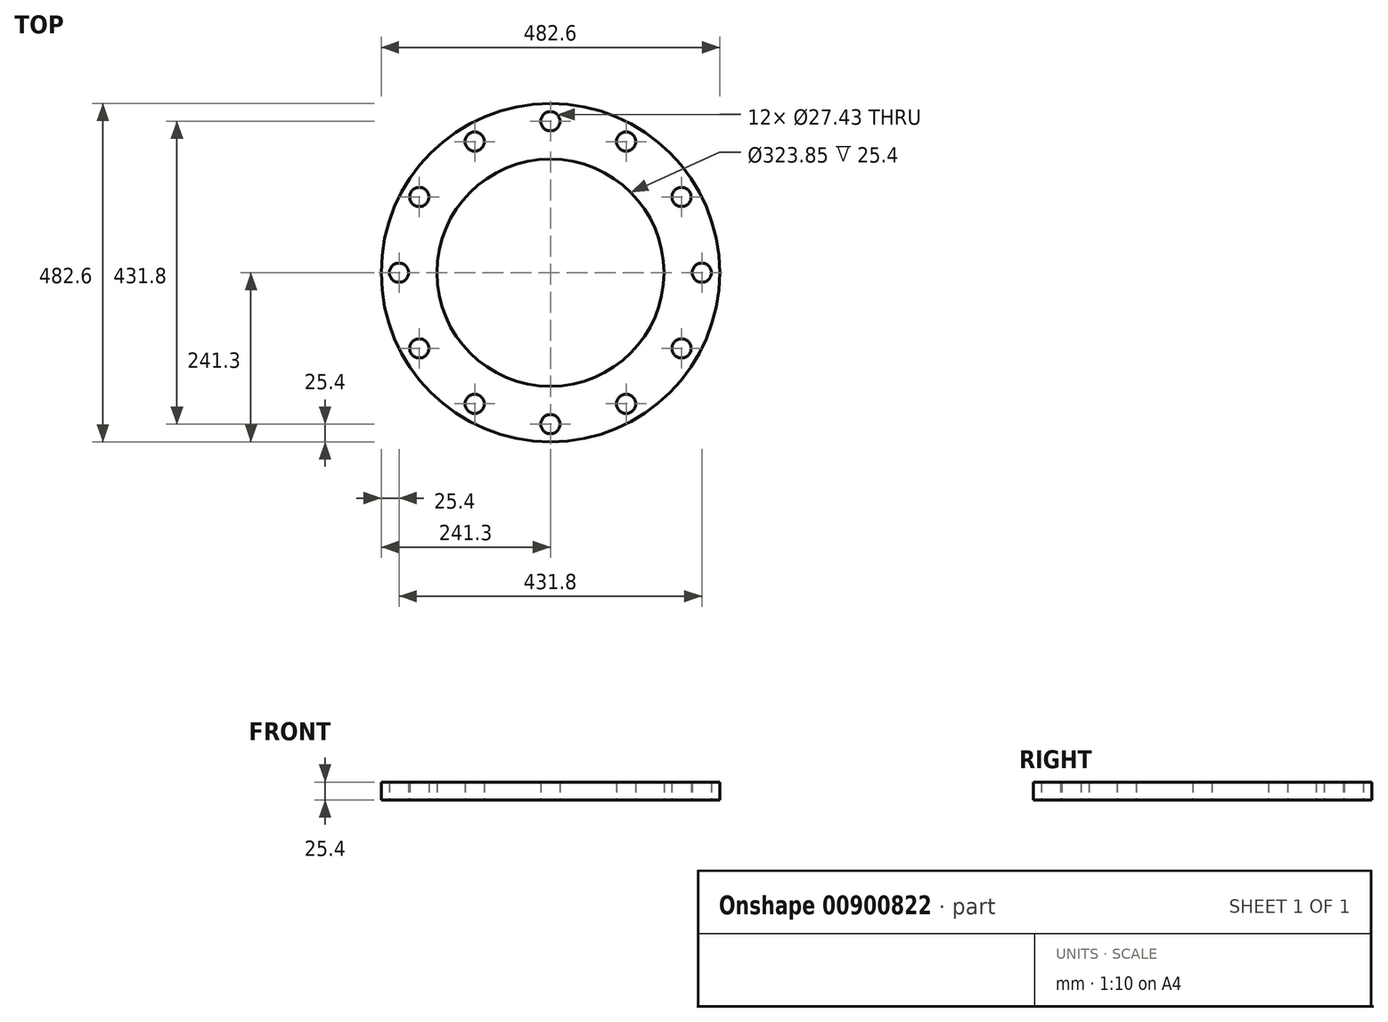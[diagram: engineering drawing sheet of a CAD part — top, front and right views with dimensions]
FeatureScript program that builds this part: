
annotation { "Feature Type Name" : "Feature", "Feature Type Description" : "" }
export const myFeature = defineFeature(function(context is Context, id is Id, definition is map)
    precondition{}
    {
        {
            var Q0;
            Q0=qCreatedBy(makeId("Top.planeOp"),FACE);
            var sketch = newSketch(context, id + "F0", { "sketchPlane" : qUnion([Q0])});
            skCircle(sketch, "E0", {"center": v(0, 0) * mm, "radius": 161.93 * mm});
            skCircle(sketch, "E1", {"center": v(0, 0) * mm, "radius": 241.3 * mm});
            skCircle(sketch, "E2", {"center": v(0, 0) * mm, "radius": 215.9 * mm});
            skLineSegment(sketch, "E3", {"start": v(0, 0) * mm, "end": v(-107.95, -186.97) * mm});
            skCircle(sketch, "E4", {"center": v(-107.95, -186.97) * mm, "radius": 13.72 * mm});
            skCircle(sketch, "E5.1.0", {"center": v(0, -215.9) * mm, "radius": 13.72 * mm});
            skCircle(sketch, "E5.2.0", {"center": v(107.95, -186.97) * mm, "radius": 13.72 * mm});
            skCircle(sketch, "E5.3.0", {"center": v(186.97, -107.95) * mm, "radius": 13.72 * mm});
            skCircle(sketch, "E5.4.0", {"center": v(215.9, 0) * mm, "radius": 13.72 * mm});
            skCircle(sketch, "E5.5.0", {"center": v(186.97, 107.95) * mm, "radius": 13.72 * mm});
            skCircle(sketch, "E5.6.0", {"center": v(107.95, 186.97) * mm, "radius": 13.72 * mm});
            skCircle(sketch, "E5.7.0", {"center": v(0, 215.9) * mm, "radius": 13.72 * mm});
            skCircle(sketch, "E5.8.0", {"center": v(-107.95, 186.97) * mm, "radius": 13.72 * mm});
            skCircle(sketch, "E5.9.0", {"center": v(-186.97, 107.95) * mm, "radius": 13.72 * mm});
            skCircle(sketch, "E5.10.0", {"center": v(-215.9, 0) * mm, "radius": 13.72 * mm});
            skCircle(sketch, "E5.11.0", {"center": v(-186.97, -107.95) * mm, "radius": 13.72 * mm});
            skSolve(sketch);
        }
        {
            var Q0;
            Q0 = qSketchRegion(id + "F0", true);
            var Q1;
            Q1=makeQuery(id+"F0.imprint","IMPRINT",FACE,{"disambiguationData":[TD([[makeQuery(id+"F0.imprint","IMPRINT",EDGE,{"derivedFrom":sQuery(id+"F0.wireOp",EDGE,"E0")}),-1.0]])]});
            extrude(context, id + "F1", {"entities" : qUnion([Q0, Q1]), "depth" : 25.4 * mm, "offsetDistance" : 25.4 * mm});
        }
    });
